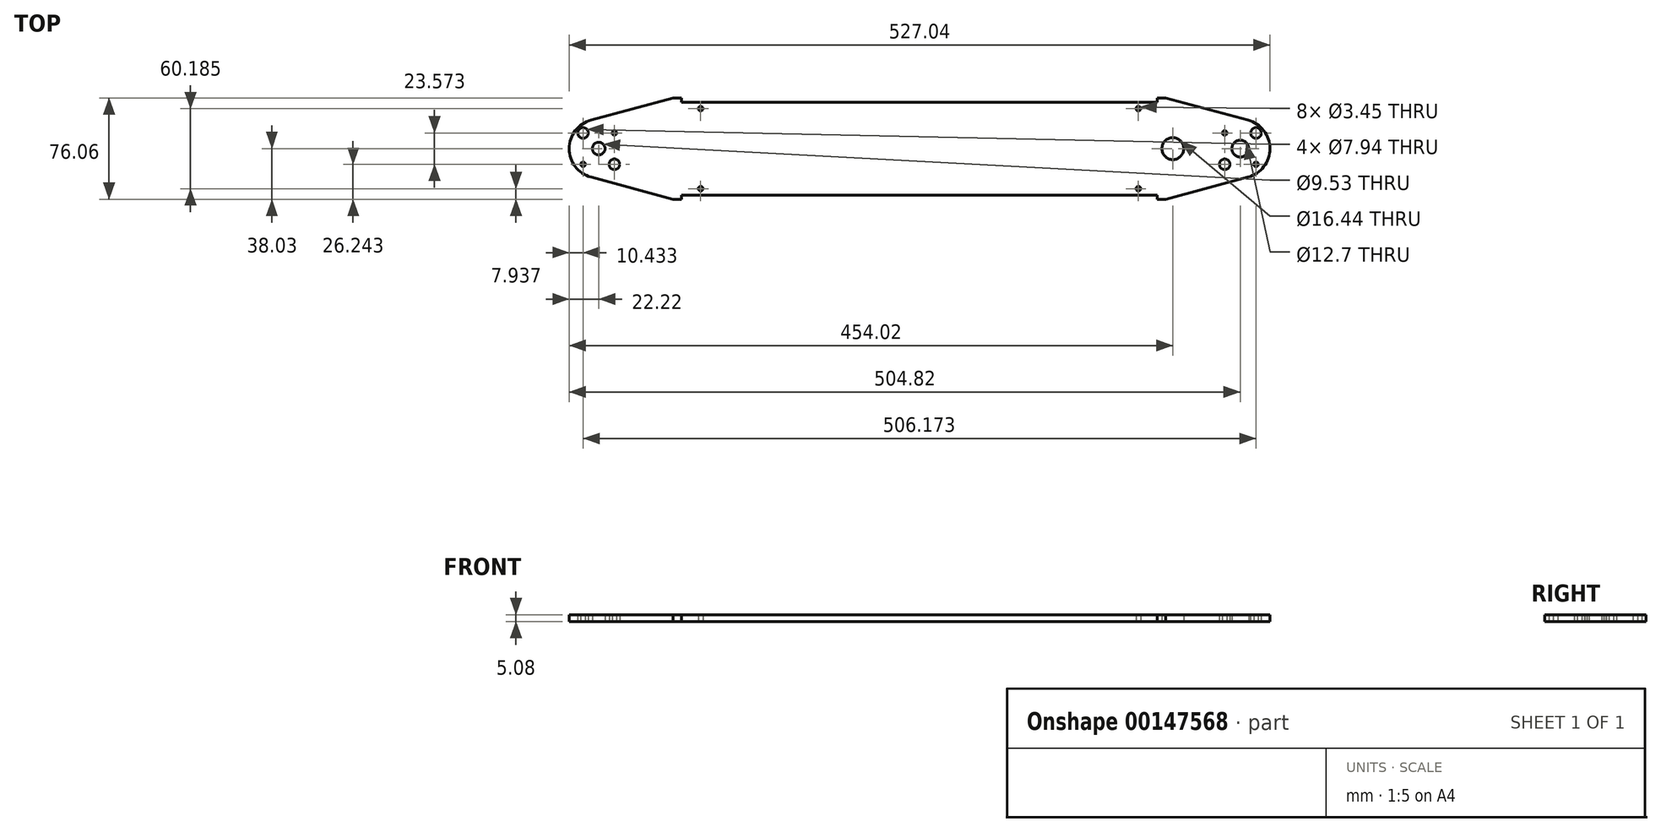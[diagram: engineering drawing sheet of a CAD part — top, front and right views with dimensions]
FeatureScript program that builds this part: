
annotation { "Feature Type Name" : "Feature", "Feature Type Description" : "" }
export const myFeature = defineFeature(function(context is Context, id is Id, definition is map)
    precondition{}
    {
        {
            var Q0;
            Q0=qCreatedBy(makeId("Top.planeOp"),FACE);
            var sketch = newSketch(context, id + "F0", { "sketchPlane" : qUnion([Q0])});
            skPoint(sketch, "E0.rect.middle", {"position": v(0, 0) * mm});
            skCircle(sketch, "E1", {"center": v(0, 0) * mm, "radius": 11.11 * mm, "construction": true});
            skLineSegment(sketch, "E2.bottom", {"start": v(11.79, 11.79) * mm, "end": v(-11.79, 11.79) * mm, "construction": true});
            skLineSegment(sketch, "E2.left", {"start": v(11.79, 11.79) * mm, "end": v(11.79, -11.79) * mm, "construction": true});
            skLineSegment(sketch, "E2.right", {"start": v(-11.79, 11.79) * mm, "end": v(-11.79, -11.79) * mm, "construction": true});
            skCircle(sketch, "E3", {"center": v(11.79, 11.79) * mm, "radius": 5.56 * mm, "construction": true});
            skCircle(sketch, "E4", {"center": v(-11.79, 11.79) * mm, "radius": 1.73 * mm});
            skCircle(sketch, "E5", {"center": v(11.79, 11.79) * mm, "radius": 3.97 * mm});
            skCircle(sketch, "E6", {"center": v(11.79, -11.79) * mm, "radius": 1.73 * mm});
            skCircle(sketch, "E7", {"center": v(-11.79, -11.79) * mm, "radius": 3.97 * mm});
            skArc(sketch, "E8", {"start": v(-488.35, 21.47) * mm, "mid": v(-504.83, 0) * mm, "end": v(-488.35, -21.47) * mm});
            skLineSegment(sketch, "E9.bottom", {"start": v(-494.39, 11.79) * mm, "end": v(-470.81, 11.79) * mm, "construction": true});
            skLineSegment(sketch, "E9.top", {"start": v(-494.39, -11.79) * mm, "end": v(-470.81, -11.79) * mm, "construction": true});
            skLineSegment(sketch, "E9.left", {"start": v(-494.39, 11.79) * mm, "end": v(-494.39, -11.79) * mm, "construction": true});
            skLineSegment(sketch, "E9.right", {"start": v(-470.81, 11.79) * mm, "end": v(-470.81, -11.79) * mm, "construction": true});
            skCircle(sketch, "E10", {"center": v(-470.81, 11.79) * mm, "radius": 1.73 * mm});
            skCircle(sketch, "E11", {"center": v(-482.6, 0) * mm, "radius": 4.76 * mm});
            skCircle(sketch, "E12", {"center": v(-494.39, 11.79) * mm, "radius": 3.97 * mm});
            skCircle(sketch, "E13", {"center": v(-494.39, -11.79) * mm, "radius": 1.73 * mm});
            skCircle(sketch, "E14", {"center": v(-470.81, -11.79) * mm, "radius": 3.97 * mm});
            skLineSegment(sketch, "E15", {"start": v(0, 0) * mm, "end": v(-482.6, 0) * mm, "construction": true});
            skLineSegment(sketch, "E16", {"start": v(-488.35, -21.47) * mm, "end": v(-426.54, -38.03) * mm});
            skLineSegment(sketch, "E17", {"start": v(-488.35, 21.47) * mm, "end": v(-426.54, 38.03) * mm});
            skLineSegment(sketch, "E18", {"start": v(-420.2, -34.86) * mm, "end": v(-62.4, -34.86) * mm});
            skLineSegment(sketch, "E19", {"start": v(-420.2, 34.86) * mm, "end": v(-62.4, 34.86) * mm});
            skLineSegment(sketch, "E20", {"start": v(-420.2, 38.03) * mm, "end": v(-420.2, 34.86) * mm});
            skLineSegment(sketch, "E21", {"start": v(-420.2, 38.03) * mm, "end": v(-426.54, 38.03) * mm});
            skLineSegment(sketch, "E22", {"start": v(-420.2, -34.86) * mm, "end": v(-420.2, -38.03) * mm});
            skLineSegment(sketch, "E23", {"start": v(-420.2, -38.03) * mm, "end": v(-426.54, -38.03) * mm});
            skLineSegment(sketch, "E24", {"start": v(-62.4, -34.86) * mm, "end": v(-62.4, -38.03) * mm});
            skLineSegment(sketch, "E25", {"start": v(-62.4, -38.03) * mm, "end": v(-56.06, -38.03) * mm});
            skLineSegment(sketch, "E26", {"start": v(-62.4, 34.86) * mm, "end": v(-62.4, 38.03) * mm});
            skLineSegment(sketch, "E27", {"start": v(-62.4, 38.03) * mm, "end": v(-56.06, 38.03) * mm});
            skLineSegment(sketch, "E28", {"start": v(-56.06, -38.03) * mm, "end": v(5.75, -21.47) * mm});
            skLineSegment(sketch, "E29", {"start": v(5.75, 21.47) * mm, "end": v(-56.06, 38.03) * mm});
            skArc(sketch, "E30", {"start": v(5.75, -21.47) * mm, "mid": v(22.23, 0) * mm, "end": v(5.75, 21.47) * mm});
            skLineSegment(sketch, "E31", {"start": v(-420.2, 34.86) * mm, "end": v(-420.2, 30.1) * mm, "construction": true});
            skLineSegment(sketch, "E32", {"start": v(-420.2, 30.1) * mm, "end": v(-405.9, 30.1) * mm, "construction": true});
            skLineSegment(sketch, "E33", {"start": v(-420.2, -34.86) * mm, "end": v(-420.2, -30.1) * mm, "construction": true});
            skLineSegment(sketch, "E34", {"start": v(-420.2, -30.1) * mm, "end": v(-405.9, -30.1) * mm, "construction": true});
            skLineSegment(sketch, "E35", {"start": v(-62.4, -34.86) * mm, "end": v(-62.4, -30.1) * mm, "construction": true});
            skLineSegment(sketch, "E36", {"start": v(-62.4, -30.1) * mm, "end": v(-76.7, -30.1) * mm, "construction": true});
            skLineSegment(sketch, "E37", {"start": v(-62.4, 34.86) * mm, "end": v(-62.4, 30.1) * mm, "construction": true});
            skLineSegment(sketch, "E38", {"start": v(-62.4, 30.1) * mm, "end": v(-76.7, 30.1) * mm, "construction": true});
            skCircle(sketch, "E39", {"center": v(-405.9, 30.1) * mm, "radius": 1.73 * mm});
            skCircle(sketch, "E40", {"center": v(-76.7, 30.1) * mm, "radius": 1.73 * mm});
            skCircle(sketch, "E41", {"center": v(-76.7, -30.1) * mm, "radius": 1.73 * mm});
            skCircle(sketch, "E42", {"center": v(-405.9, -30.1) * mm, "radius": 1.73 * mm});
            skLineSegment(sketch, "E43", {"start": v(-11.79, -11.79) * mm, "end": v(11.79, -11.79) * mm, "construction": true});
            skLineSegment(sketch, "E44", {"start": v(-241.3, -34.86) * mm, "end": v(-241.3, 0) * mm, "construction": true});
            skLineSegment(sketch, "E45", {"start": v(-241.3, 0) * mm, "end": v(-241.3, 34.86) * mm, "construction": true});
            skCircle(sketch, "E46", {"center": v(-50.8, 0) * mm, "radius": 8.22 * mm});
            skCircle(sketch, "E47", {"center": v(0, 0) * mm, "radius": 6.35 * mm});
            skCircle(sketch, "E48", {"center": v(-494.39, 11.79) * mm, "radius": 5.56 * mm, "construction": true});
            skLineSegment(sketch, "E49", {"start": v(-488.35, 21.47) * mm, "end": v(-457.45, 21.47) * mm, "construction": true});
            skLineSegment(sketch, "E50", {"start": v(-457.45, 21.47) * mm, "end": v(-457.45, 29.75) * mm, "construction": true});
            skSolve(sketch);
        }
        {
            var Q0;
            Q0=qSketchRegion(id+"F0",true);
            extrude(context, id + "F1", {"entities" : qUnion([Q0]), "depth" : 5.08 * mm});
        }
    });
